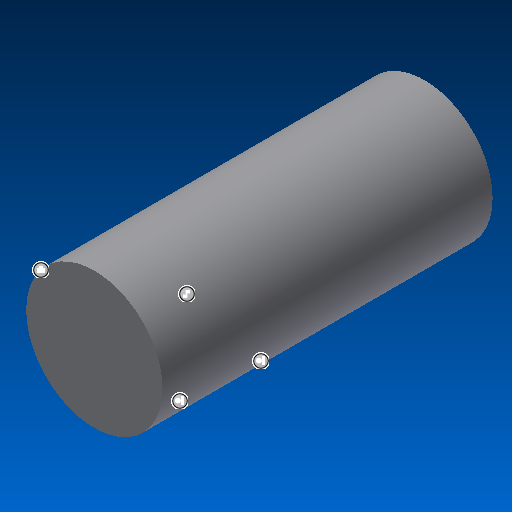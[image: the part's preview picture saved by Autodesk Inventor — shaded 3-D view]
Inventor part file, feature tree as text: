
AUTODESK INVENTOR PART (.ipt)
format: ipt  version: 2019 (Build 230136000, 136)  size: 107,520 bytes
history: native  units: mm
features: extrude x1, sketch x1
ambient origin geometry x8: Origin, YZ Plane, XZ Plane, XY Plane, X Axis, Y Axis, Z Axis, Center Point
bodies: Solid1 (feature_tree)
feature tree (2):
  extrude  "Extrusion1"  TaperAngle=0.0deg  [1 undecoded]
  sketch  "Sketch1"  dims[d2=0.0mm d3=0.0mm d4=0.0mm d9=0.0mm d10=0.0mm]
note: 1 required parameter value undecoded (feature->parameter linkage not recoverable at this tier; creation-order binding heuristic only, values carry confidence <= 0.55)
